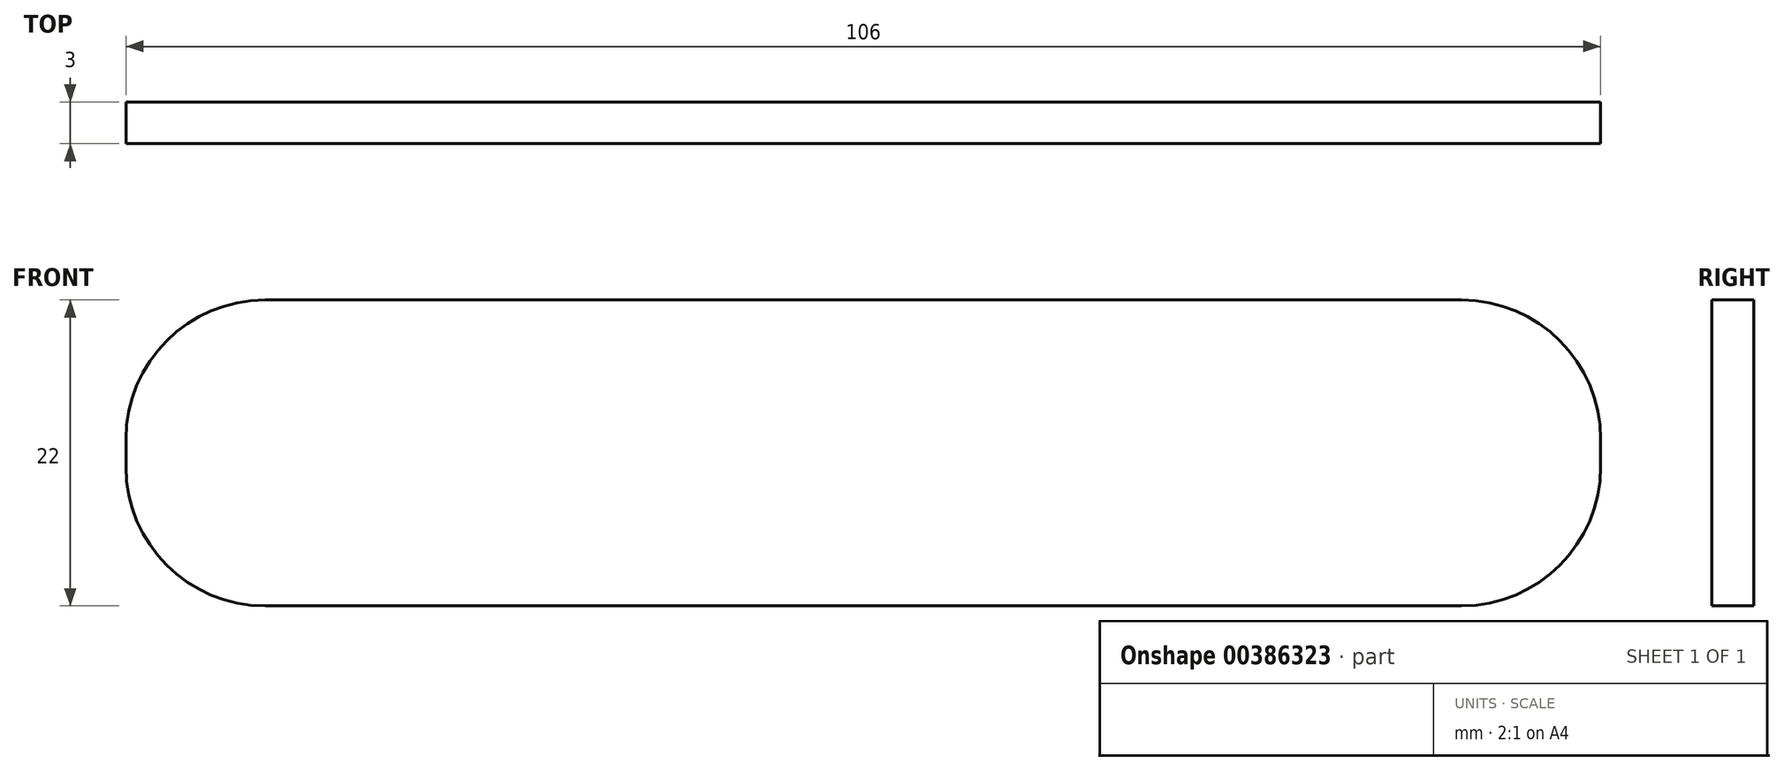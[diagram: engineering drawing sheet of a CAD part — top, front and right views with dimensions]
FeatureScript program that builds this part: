
annotation { "Feature Type Name" : "Feature", "Feature Type Description" : "" }
export const myFeature = defineFeature(function(context is Context, id is Id, definition is map)
    precondition{}
    {
        {
            var Q0;
            Q0=qCreatedBy(makeId("Front.planeOp"),FACE);
            var sketch = newSketch(context, id + "F0", { "sketchPlane" : qUnion([Q0])});
            skLineSegment(sketch, "E0.bottom", {"start": v(-50.37, 12.02) * mm, "end": v(55.63, 12.02) * mm});
            skLineSegment(sketch, "E0.top", {"start": v(-50.37, -9.98) * mm, "end": v(55.63, -9.98) * mm});
            skLineSegment(sketch, "E0.left", {"start": v(-50.37, 12.02) * mm, "end": v(-50.37, -9.98) * mm});
            skLineSegment(sketch, "E0.right", {"start": v(55.63, 12.02) * mm, "end": v(55.63, -9.98) * mm});
            skSolve(sketch);
        }
        {
            var Q0;
            Q0=makeQuery(id+"F0.imprint","IMPRINT",FACE,{"disambiguationData":[TD([[makeQuery(id+"F0.imprint","IMPRINT",EDGE,{"derivedFrom":sQuery(id+"F0.wireOp",EDGE,"E0.bottom")}),-1.0]])]});
            extrude(context, id + "F1", {"entities" : qUnion([Q0]), "depth" : 3 * mm});
        }
        {
            var Q0;
            Q0=makeQuery(id+"F1.opExtrude","SWEPT_EDGE",EDGE,{"disambiguationData":[OSD([sQuery(id+"F0.wireOp",EDGE,"E0.bottom"),sQuery(id+"F0.wireOp",EDGE,"E0.right")])]});
            var Q1;
            Q1=makeQuery(id+"F1.opExtrude","SWEPT_EDGE",EDGE,{"disambiguationData":[OSD([sQuery(id+"F0.wireOp",EDGE,"E0.top"),sQuery(id+"F0.wireOp",EDGE,"E0.right")])]});
            var Q2;
            Q2=makeQuery(id+"F1.opExtrude","SWEPT_EDGE",EDGE,{"disambiguationData":[OSD([sQuery(id+"F0.wireOp",EDGE,"E0.bottom"),sQuery(id+"F0.wireOp",EDGE,"E0.left")])]});
            var Q3;
            Q3=makeQuery(id+"F1.opExtrude","SWEPT_EDGE",EDGE,{"disambiguationData":[OSD([sQuery(id+"F0.wireOp",EDGE,"E0.top"),sQuery(id+"F0.wireOp",EDGE,"E0.left")])]});
            fillet(context, id + "F2", {"entities" : qUnion([Q0, Q1, Q2, Q3]), "radius" : 10 * mm, "tangentPropagation" : true, "allowEdgeOverflow" : false});
        }
    });
